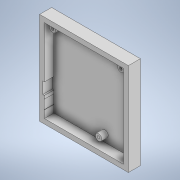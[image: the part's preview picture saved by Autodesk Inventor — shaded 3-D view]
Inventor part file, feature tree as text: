
AUTODESK INVENTOR PART (.ipt)
format: ipt  version: 2021 (Build 250183000, 183)  size: 135,168 bytes
history: native  units: mm
features: extrude x3, sketch x2
ambient origin geometry x8: Origin, YZ Plane, XZ Plane, XY Plane, X Axis, Y Axis, Z Axis, Center Point
bodies: Solid1 (feature_tree)
feature tree (5):
  sketch  "Sketch1"  dims[d0=2.0mm d1=4.0mm]
  extrude  "Extrusion1"  Depth=4.0mm
  extrude  "Extrusion2"  Depth=3.0mm TaperAngle=0.0deg
  extrude  "Extrusion4"  Depth=8.0mm
  sketch  "Sketch2"  dims[d2=15.0mm d3=0.0mm d4=3.0mm d5=0.0mm d8=8.0mm d9=8.0mm d10=8.0mm d11=8.0mm d12=0.0mm]
